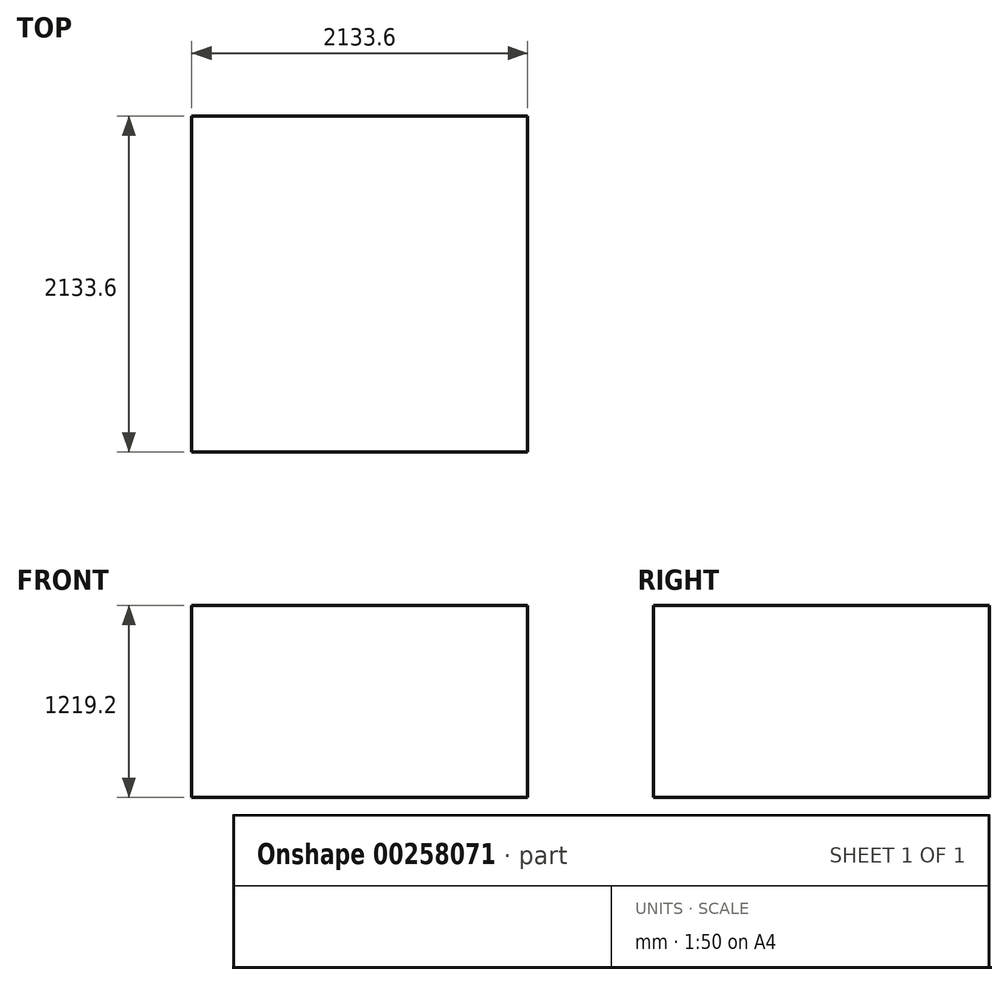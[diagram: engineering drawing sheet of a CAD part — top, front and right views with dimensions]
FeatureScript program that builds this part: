
annotation { "Feature Type Name" : "Feature", "Feature Type Description" : "" }
export const myFeature = defineFeature(function(context is Context, id is Id, definition is map)
    precondition{}
    {
        {
            var Q0;
            Q0=qCreatedBy(makeId("Front.planeOp"),FACE);
            var sketch = newSketch(context, id + "F0", { "sketchPlane" : qUnion([Q0])});
            skLineSegment(sketch, "E0.bottom", {"start": v(1066.8, -609.6) * mm, "end": v(-1066.8, -609.6) * mm});
            skLineSegment(sketch, "E0.top", {"start": v(1066.8, 609.6) * mm, "end": v(-1066.8, 609.6) * mm});
            skLineSegment(sketch, "E0.left", {"start": v(1066.8, -609.6) * mm, "end": v(1066.8, 609.6) * mm});
            skLineSegment(sketch, "E0.right", {"start": v(-1066.8, -609.6) * mm, "end": v(-1066.8, 609.6) * mm});
            skPoint(sketch, "E0.middle", {"position": v(0, 0) * mm});
            skSolve(sketch);
        }
        {
            var Q0;
            Q0 = qSketchRegion(id + "F0", true);
            extrude(context, id + "F1", {"entities" : qUnion([Q0]), "depth" : 2133.6 * mm});
        }
    });
